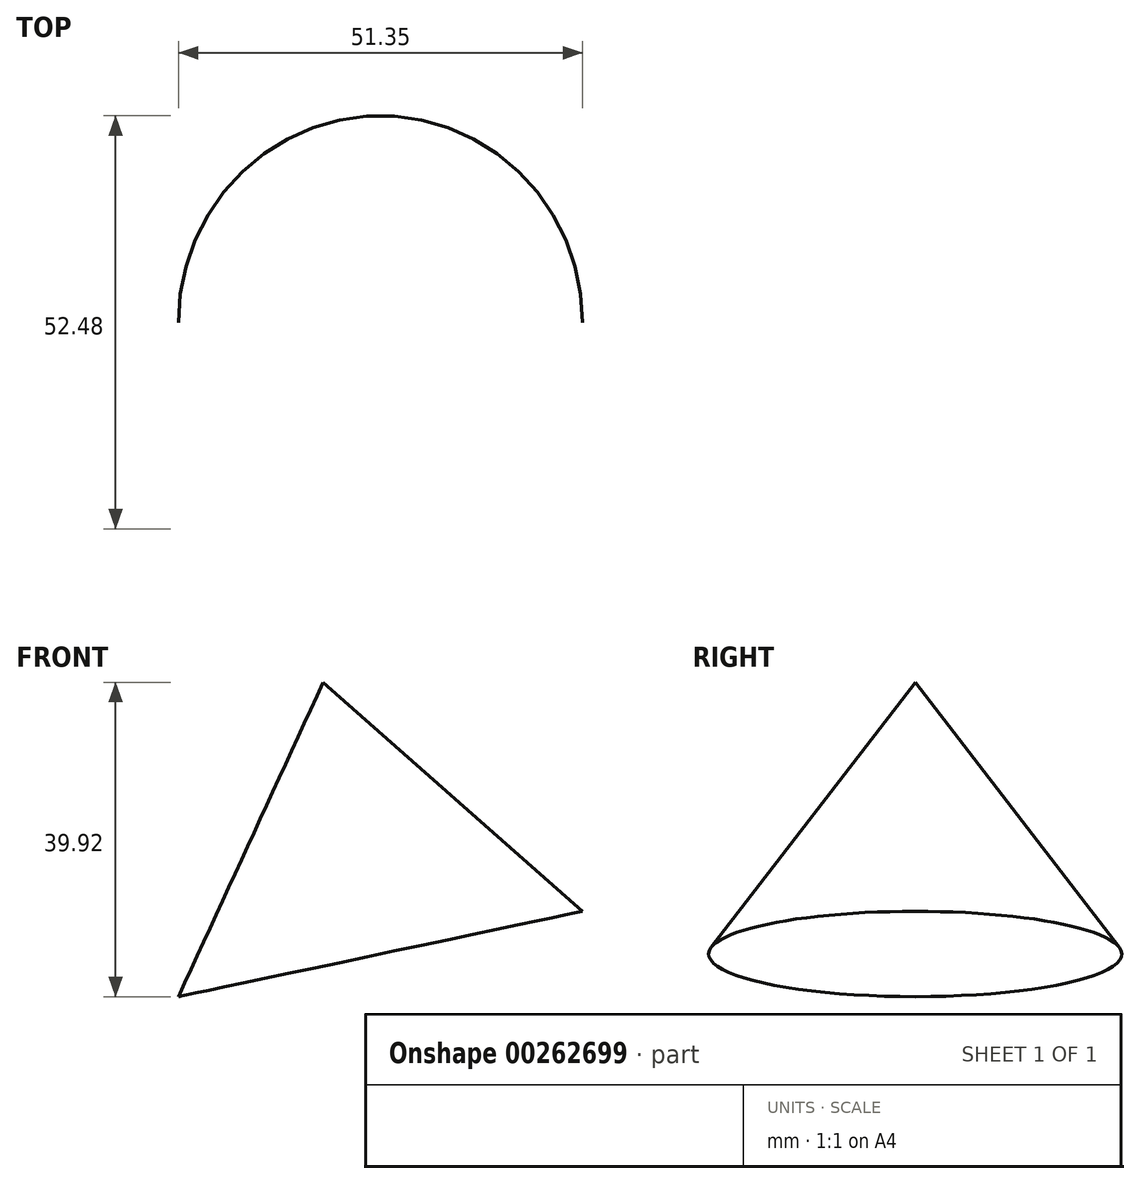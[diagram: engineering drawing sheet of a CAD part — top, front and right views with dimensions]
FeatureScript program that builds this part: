
annotation { "Feature Type Name" : "Feature", "Feature Type Description" : "" }
export const myFeature = defineFeature(function(context is Context, id is Id, definition is map)
    precondition{}
    {
        {
            var Q0;
            Q0=qCreatedBy(makeId("Front.planeOp"),FACE);
            var sketch = newSketch(context, id + "F0", { "sketchPlane" : qUnion([Q0])});
            skLineSegment(sketch, "E0", {"start": v(-21.22, 48.5) * mm, "end": v(-13.94, 14.01) * mm});
            skLineSegment(sketch, "E1", {"start": v(-13.94, 14.01) * mm, "end": v(11.74, 19.43) * mm});
            skLineSegment(sketch, "E2", {"start": v(-21.22, 48.5) * mm, "end": v(11.74, 19.43) * mm});
            skSolve(sketch);
        }
        {
            var Q0;
            Q0=makeQuery(id+"F0.imprint","IMPRINT",FACE,{"disambiguationData":[TD([[makeQuery(id+"F0.imprint","IMPRINT",EDGE,{"derivedFrom":sQuery(id+"F0.wireOp",EDGE,"E0")}),1.0]])]});
            var Q1;
            Q1=sQuery(id+"F0.wireOp",EDGE,"E0");
            revolve(context, id + "F1", {"entities" : qUnion([Q0]), "axis" : qUnion([Q1]), "revolveType" : RevolveType.FULL});
        }
    });
